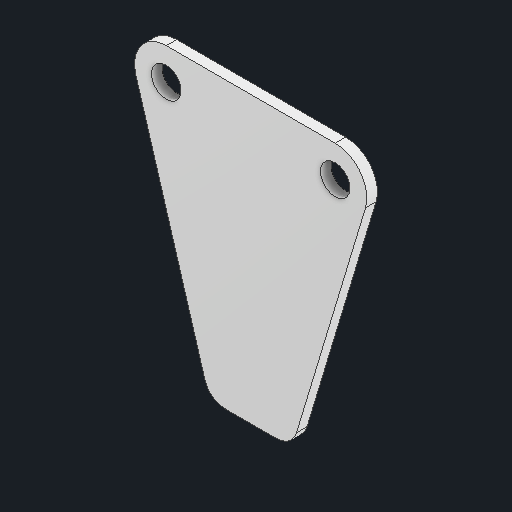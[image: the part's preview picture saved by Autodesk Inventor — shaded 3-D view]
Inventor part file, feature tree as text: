
AUTODESK INVENTOR PART (.ipt)
format: ipt  version: 2025 (Build 290162000, 162)  size: 101,376 bytes
history: native  units: in
note: dims shown in document units (in); Inventor stores cm internally (conversion verified against a paired STEP export)
features: extrude x1, sketch x1
ambient origin geometry x8: Origin, YZ Plane, XZ Plane, XY Plane, X Axis, Y Axis, Z Axis, Center Point
bodies: Solid1 (feature_tree)
feature tree (2):
  extrude  "Extrusion1"  Depth=0.0625in TaperAngle=0.0deg
  sketch  "Sketch1"  dims[d0=1.5in d1=0.125in d2=0.1875in d3=0.1875in d4=0.0625in d5=0.0in]
